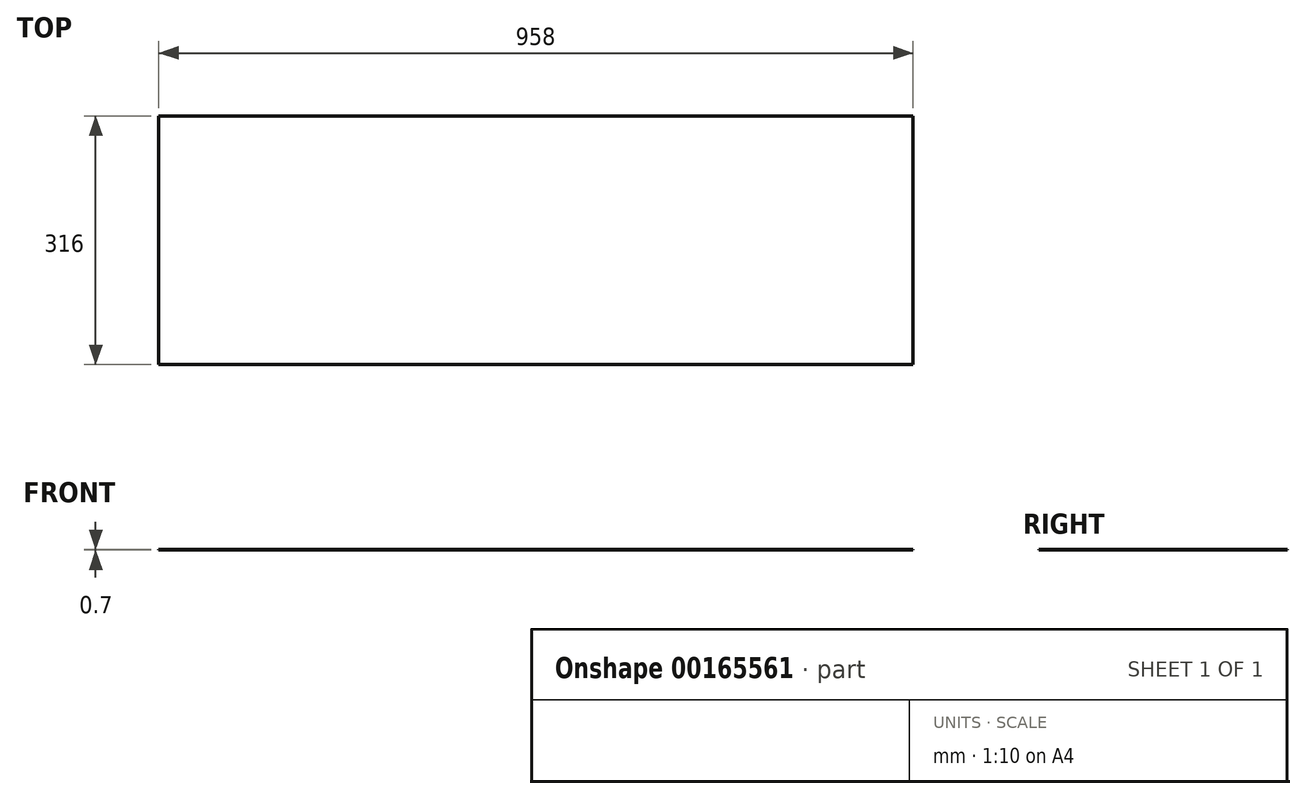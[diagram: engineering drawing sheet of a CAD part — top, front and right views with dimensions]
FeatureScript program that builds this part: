
annotation { "Feature Type Name" : "Feature", "Feature Type Description" : "" }
export const myFeature = defineFeature(function(context is Context, id is Id, definition is map)
    precondition{}
    {
        {
            var Q0;
            Q0=qCreatedBy(makeId("Top.planeOp"),FACE);
            var sketch = newSketch(context, id + "F0", { "sketchPlane" : qUnion([Q0])});
            skLineSegment(sketch, "E0.bottom", {"start": v(479, 158) * mm, "end": v(-479, 158) * mm});
            skLineSegment(sketch, "E0.top", {"start": v(479, -158) * mm, "end": v(-479, -158) * mm});
            skLineSegment(sketch, "E0.left", {"start": v(479, 158) * mm, "end": v(479, -158) * mm});
            skLineSegment(sketch, "E0.right", {"start": v(-479, 158) * mm, "end": v(-479, -158) * mm});
            skPoint(sketch, "E0.middle", {"position": v(0, 0) * mm});
            skSolve(sketch);
        }
        {
            var Q0;
            Q0=makeQuery(id+"F0.imprint","IMPRINT",FACE,{"disambiguationData":[TD([[makeQuery(id+"F0.imprint","IMPRINT",EDGE,{"derivedFrom":sQuery(id+"F0.wireOp",EDGE,"E0.bottom")}),1.0]])]});
            extrude(context, id + "F1", {"entities" : qUnion([Q0]), "depth" : 0.7 * mm});
        }
    });
